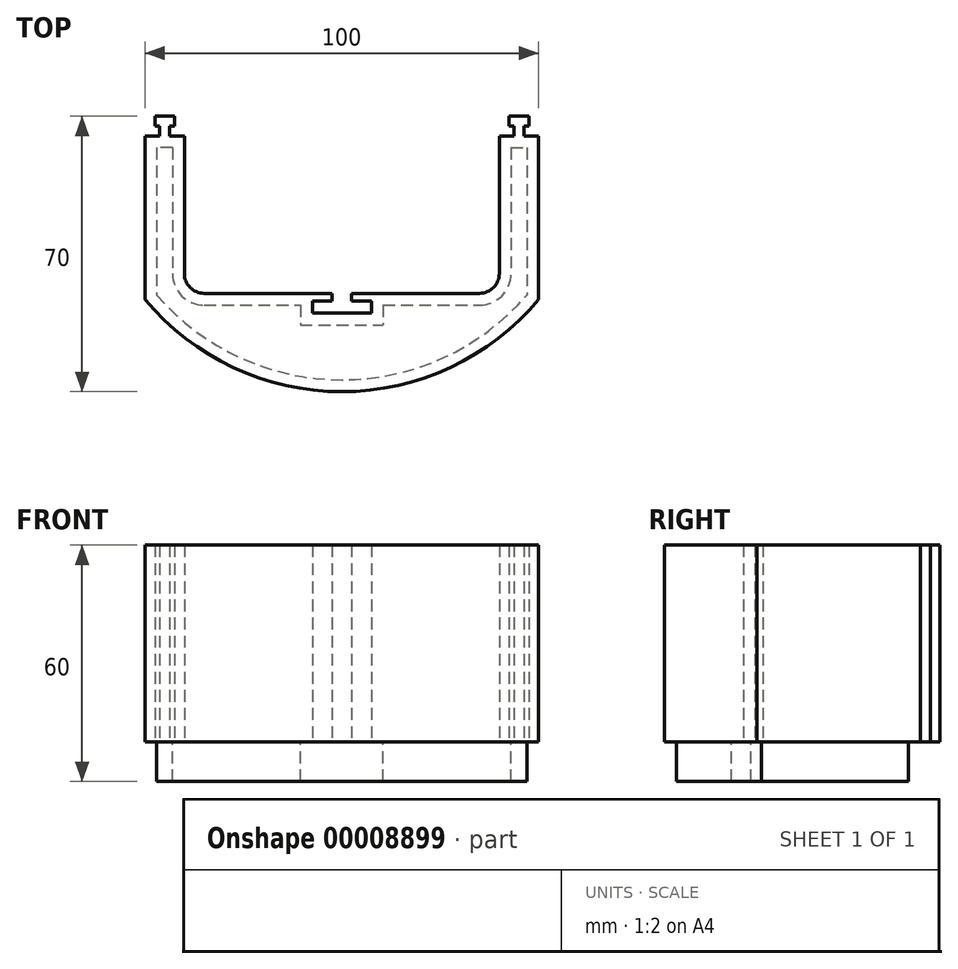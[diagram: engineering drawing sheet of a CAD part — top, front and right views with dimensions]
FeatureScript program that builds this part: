
annotation { "Feature Type Name" : "Feature", "Feature Type Description" : "" }
export const myFeature = defineFeature(function(context is Context, id is Id, definition is map)
    precondition{}
    {
        {
            var Q0;
            Q0=qCreatedBy(makeId("Top.planeOp"),FACE);
            var sketch = newSketch(context, id + "F0", { "sketchPlane" : qUnion([Q0])});
            skCircle(sketch, "E0", {"center": v(0, 0) * mm, "radius": 65 * mm});
            skLineSegment(sketch, "E1", {"start": v(0, 0) * mm, "end": v(0, -32.05) * mm});
            skLineSegment(sketch, "E2.0", {"start": v(-40, 0) * mm, "end": v(-40, -35) * mm});
            skLineSegment(sketch, "E3.0", {"start": v(40, 0) * mm, "end": v(40, -35) * mm});
            skLineSegment(sketch, "E4.0", {"start": v(50, 0) * mm, "end": v(50, -41.53) * mm});
            skLineSegment(sketch, "E5.0", {"start": v(-50, 0) * mm, "end": v(-50, -41.53) * mm});
            skLineSegment(sketch, "E6", {"start": v(0, 0) * mm, "end": v(-50, 0) * mm});
            skLineSegment(sketch, "E7", {"start": v(0, 0) * mm, "end": v(50, 0) * mm});
            skLineSegment(sketch, "E8", {"start": v(-35, -40) * mm, "end": v(35, -40) * mm});
            skPoint(sketch, "E9.visualSharp", {"position": v(-40, -40) * mm});
            skArc(sketch, "E9.filletArc", {"start": v(-40, -35) * mm, "mid": v(-38.54, -38.54) * mm, "end": v(-35, -40) * mm});
            skPoint(sketch, "E10.visualSharp", {"position": v(40, -40) * mm});
            skArc(sketch, "E10.filletArc", {"start": v(35, -40) * mm, "mid": v(38.54, -38.54) * mm, "end": v(40, -35) * mm});
            skLineSegment(sketch, "E11", {"start": v(0, -40) * mm, "end": v(0, -45) * mm});
            skLineSegment(sketch, "E12.0", {"start": v(-2.5, -40) * mm, "end": v(-2.5, -42) * mm});
            skLineSegment(sketch, "E13.0", {"start": v(2.5, -40) * mm, "end": v(2.5, -42) * mm});
            skLineSegment(sketch, "E14.0", {"start": v(-7.5, -42) * mm, "end": v(-7.5, -45) * mm});
            skLineSegment(sketch, "E15.0", {"start": v(7.5, -42) * mm, "end": v(7.5, -45) * mm});
            skLineSegment(sketch, "E16", {"start": v(7.5, -45) * mm, "end": v(-7.5, -45) * mm});
            skLineSegment(sketch, "E17.0", {"start": v(7.5, -42) * mm, "end": v(2.5, -42) * mm});
            skLineSegment(sketch, "E18.trimOffspring", {"start": v(-2.5, -42) * mm, "end": v(-7.5, -42) * mm});
            skLineSegment(sketch, "E19", {"start": v(-50, 0) * mm, "end": v(-50, 5) * mm});
            skLineSegment(sketch, "E20.0", {"start": v(-43.75, 0) * mm, "end": v(-43.75, 2.5) * mm});
            skLineSegment(sketch, "E21.0", {"start": v(-46.25, 0) * mm, "end": v(-46.25, 2.5) * mm});
            skLineSegment(sketch, "E22.0", {"start": v(-47.5, 2.5) * mm, "end": v(-47.5, 5) * mm});
            skLineSegment(sketch, "E23.0", {"start": v(-42.5, 2.5) * mm, "end": v(-42.5, 5) * mm});
            skLineSegment(sketch, "E24", {"start": v(-47.5, 5) * mm, "end": v(-42.5, 5) * mm});
            skLineSegment(sketch, "E25.0", {"start": v(-47.5, 2.5) * mm, "end": v(-46.25, 2.5) * mm});
            skLineSegment(sketch, "E26.trimOffspring", {"start": v(-43.75, 2.5) * mm, "end": v(-42.5, 2.5) * mm});
            skLineSegment(sketch, "E27", {"start": v(40, 0) * mm, "end": v(40, 5) * mm});
            skLineSegment(sketch, "E28.0", {"start": v(46.25, 0) * mm, "end": v(46.25, 2.5) * mm});
            skLineSegment(sketch, "E29.0", {"start": v(43.75, 0) * mm, "end": v(43.75, 2.5) * mm});
            skLineSegment(sketch, "E30.0", {"start": v(42.5, 2.5) * mm, "end": v(42.5, 5) * mm});
            skLineSegment(sketch, "E31.0", {"start": v(47.5, 2.5) * mm, "end": v(47.5, 5) * mm});
            skLineSegment(sketch, "E32", {"start": v(42.5, 5) * mm, "end": v(47.5, 5) * mm});
            skLineSegment(sketch, "E33.0", {"start": v(42.5, 2.5) * mm, "end": v(43.75, 2.5) * mm});
            skLineSegment(sketch, "E34.trimOffspring", {"start": v(46.25, 2.5) * mm, "end": v(47.5, 2.5) * mm});
            skSolve(sketch);
        }
        {
            var Q0;
            {var subQ1=sQuery(id+"F0.wireOp",EDGE,"E20.0");Q0=makeQuery(id+"F0.imprint","IMPRINT",FACE,{"disambiguationData":[TD([[makeQuery(id+"F0.imprint","IMPRINT",EDGE,{"derivedFrom":subQ1}),1.0]])]});}
            var Q1;
            {var subQ10=sQuery(id+"F0.wireOp",EDGE,"E2.0");Q1=makeQuery(id+"F0.imprint","IMPRINT",FACE,{"disambiguationData":[TD([[makeQuery(id+"F0.imprint","IMPRINT",EDGE,{"derivedFrom":subQ10}),-1.0]])]});}
            var Q2;
            {var subQ1=sQuery(id+"F0.wireOp",EDGE,"E28.0");Q2=makeQuery(id+"F0.imprint","IMPRINT",FACE,{"disambiguationData":[TD([[makeQuery(id+"F0.imprint","IMPRINT",EDGE,{"derivedFrom":subQ1}),1.0]])]});}
            extrude(context, id + "F1", {"entities" : qUnion([Q0, Q1, Q2]), "depth" : 50 * mm});
        }
        {
            var Q0;
            Q0=makeQuery(id+"F1.opExtrude","CAP_FACE",FACE,{"disambiguationData":[OSD([sQuery(id+"F0.wireOp",EDGE,"E0"),sQuery(id+"F0.wireOp",EDGE,"E2.0"),sQuery(id+"F0.wireOp",EDGE,"E3.0"),sQuery(id+"F0.wireOp",EDGE,"E4.0"),sQuery(id+"F0.wireOp",EDGE,"E5.0"),sQuery(id+"F0.wireOp",EDGE,"E6"),sQuery(id+"F0.wireOp",EDGE,"E7"),sQuery(id+"F0.wireOp",EDGE,"E8"),sQuery(id+"F0.wireOp",EDGE,"E9.filletArc"),sQuery(id+"F0.wireOp",EDGE,"E10.filletArc"),sQuery(id+"F0.wireOp",EDGE,"E12.0"),sQuery(id+"F0.wireOp",EDGE,"E13.0"),sQuery(id+"F0.wireOp",EDGE,"E14.0"),sQuery(id+"F0.wireOp",EDGE,"E15.0"),sQuery(id+"F0.wireOp",EDGE,"E16"),sQuery(id+"F0.wireOp",EDGE,"E17.0"),sQuery(id+"F0.wireOp",EDGE,"E18.trimOffspring"),sQuery(id+"F0.wireOp",EDGE,"E20.0"),sQuery(id+"F0.wireOp",EDGE,"E21.0"),sQuery(id+"F0.wireOp",EDGE,"E22.0"),sQuery(id+"F0.wireOp",EDGE,"E23.0"),sQuery(id+"F0.wireOp",EDGE,"E24"),sQuery(id+"F0.wireOp",EDGE,"E25.0"),sQuery(id+"F0.wireOp",EDGE,"E26.trimOffspring"),sQuery(id+"F0.wireOp",EDGE,"E28.0"),sQuery(id+"F0.wireOp",EDGE,"E29.0"),sQuery(id+"F0.wireOp",EDGE,"E30.0"),sQuery(id+"F0.wireOp",EDGE,"E31.0"),sQuery(id+"F0.wireOp",EDGE,"E32"),sQuery(id+"F0.wireOp",EDGE,"E33.0"),sQuery(id+"F0.wireOp",EDGE,"E34.trimOffspring")])],"isStart":true});
            var sketch = newSketch(context, id + "F2", { "sketchPlane" : qUnion([Q0])});
            skLineSegment(sketch, "E35", {"start": v(-46.25, 0) * mm, "end": v(-43.75, 0) * mm});
            skLineSegment(sketch, "E36", {"start": v(46.25, 0) * mm, "end": v(43.75, 0) * mm});
            skLineSegment(sketch, "E37", {"start": v(0, 0) * mm, "end": v(0, 42.5) * mm});
            skLineSegment(sketch, "E38.0", {"start": v(10, 43) * mm, "end": v(10, 48) * mm, "construction": true});
            skLineSegment(sketch, "E39.0", {"start": v(-10, 43) * mm, "end": v(-10, 48) * mm, "construction": true});
            skLineSegment(sketch, "E40", {"start": v(2.5, 40) * mm, "end": v(-2.5, 40) * mm});
            skLineSegment(sketch, "E41.0", {"start": v(-46.25, 3) * mm, "end": v(-47, 3) * mm});
            skLineSegment(sketch, "E41.1", {"start": v(-47, 3) * mm, "end": v(-47, 40.44) * mm});
            skArc(sketch, "E41.2", {"start": v(-47, 40.44) * mm, "mid": v(0, 62) * mm, "end": v(47, 40.44) * mm});
            skLineSegment(sketch, "E41.3", {"start": v(47, 3) * mm, "end": v(47, 40.44) * mm});
            skLineSegment(sketch, "E41.4", {"start": v(46.25, 3) * mm, "end": v(47, 3) * mm});
            skLineSegment(sketch, "E41.5", {"start": v(-46.25, 3) * mm, "end": v(-43.75, 3) * mm});
            skLineSegment(sketch, "E41.6", {"start": v(46.25, 3) * mm, "end": v(43.75, 3) * mm});
            skLineSegment(sketch, "E41.7", {"start": v(43, 3) * mm, "end": v(43.75, 3) * mm});
            skLineSegment(sketch, "E41.8", {"start": v(43, 3) * mm, "end": v(43, 35) * mm});
            skArc(sketch, "E41.9", {"start": v(35, 43) * mm, "mid": v(40.66, 40.66) * mm, "end": v(43, 35) * mm});
            skLineSegment(sketch, "E41.10", {"start": v(10, 43) * mm, "end": v(35, 43) * mm});
            skLineSegment(sketch, "E41.12", {"start": v(-35, 43) * mm, "end": v(-10, 43) * mm});
            skArc(sketch, "E41.13", {"start": v(-43, 35) * mm, "mid": v(-40.66, 40.66) * mm, "end": v(-35, 43) * mm});
            skLineSegment(sketch, "E41.14", {"start": v(-43, 3) * mm, "end": v(-43, 35) * mm});
            skLineSegment(sketch, "E41.15", {"start": v(-43, 3) * mm, "end": v(-43.75, 3) * mm});
            skLineSegment(sketch, "E42", {"start": v(-10.5, 48) * mm, "end": v(10.5, 48) * mm});
            skLineSegment(sketch, "E43.0", {"start": v(-10.5, 43) * mm, "end": v(-10.5, 48) * mm});
            skLineSegment(sketch, "E44.0", {"start": v(10.5, 43) * mm, "end": v(10.5, 48) * mm});
            skSolve(sketch);
        }
        {
            var Q0;
            Q0=makeQuery(id+"F2.imprint","IMPRINT",FACE,{"disambiguationData":[TD([[makeQuery(id+"F2.imprint","IMPRINT",EDGE,{"derivedFrom":sQuery(id+"F2.wireOp",EDGE,"E38.0")}),-1.0]])]});
            var Q1;
            Q1=makeQuery(id+"F2.imprint","IMPRINT",FACE,{"disambiguationData":[TD([[makeQuery(id+"F2.imprint","IMPRINT",EDGE,{"derivedFrom":sQuery(id+"F2.wireOp",EDGE,"E41.0")}),-1.0]])]});
            extrude(context, id + "F3", {"entities" : qUnion([Q0, Q1]), "operationType" : NewBodyOperationType.ADD, "depth" : 10 * mm});
        }
    });
